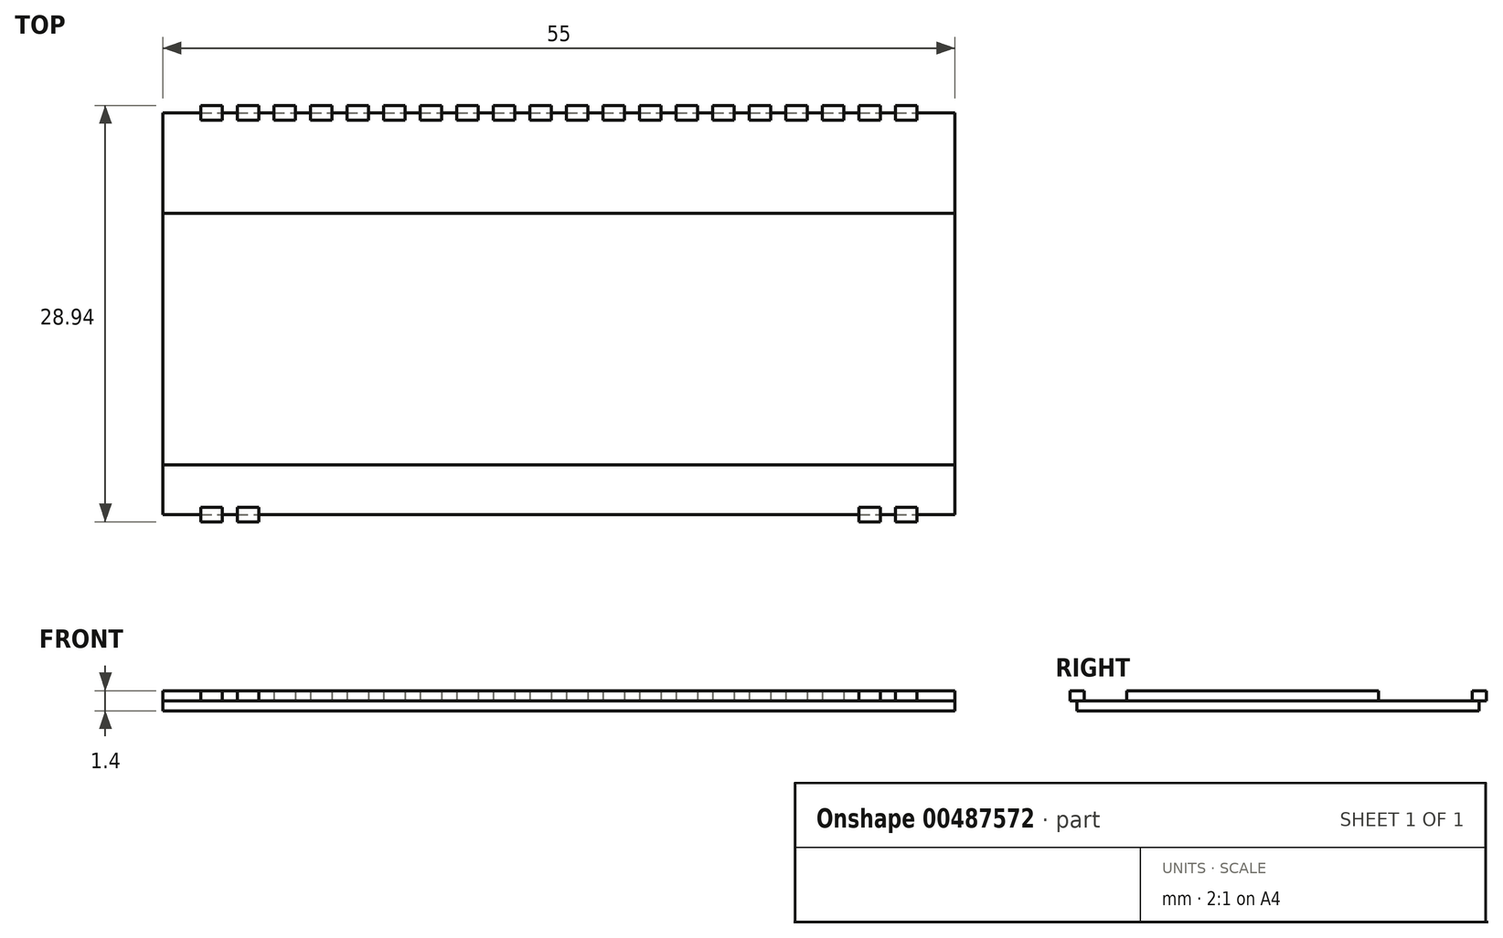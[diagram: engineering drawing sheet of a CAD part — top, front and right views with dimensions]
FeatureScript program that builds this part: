
annotation { "Feature Type Name" : "Feature", "Feature Type Description" : "" }
export const myFeature = defineFeature(function(context is Context, id is Id, definition is map)
    precondition{}
    {
        {
            var Q0;
            Q0=qCreatedBy(makeId("Top.planeOp"),FACE);
            var sketch = newSketch(context, id + "F0", { "sketchPlane" : qUnion([Q0])});
            skLineSegment(sketch, "E0.bottom", {"start": v(-27.5, 15.75) * mm, "end": v(27.5, 15.75) * mm});
            skLineSegment(sketch, "E0.top", {"start": v(-27.5, -12.2) * mm, "end": v(27.5, -12.2) * mm});
            skLineSegment(sketch, "E0.left", {"start": v(-27.5, 15.75) * mm, "end": v(-27.5, -12.2) * mm});
            skLineSegment(sketch, "E0.right", {"start": v(27.5, 15.75) * mm, "end": v(27.5, -12.2) * mm});
            skLineSegment(sketch, "E1", {"start": v(-27.5, 8.75) * mm, "end": v(27.5, 8.75) * mm});
            skLineSegment(sketch, "E2", {"start": v(-27.5, -8.75) * mm, "end": v(27.5, -8.75) * mm});
            skLineSegment(sketch, "E3.bottom", {"start": v(-24.08, 6.64) * mm, "end": v(24.08, 6.64) * mm});
            skLineSegment(sketch, "E3.top", {"start": v(-24.08, -6.63) * mm, "end": v(24.08, -6.64) * mm});
            skLineSegment(sketch, "E3.left", {"start": v(-24.09, 6.64) * mm, "end": v(-24.09, -6.64) * mm});
            skLineSegment(sketch, "E3.right", {"start": v(24.09, 6.64) * mm, "end": v(24.08, -6.64) * mm});
            skLineSegment(sketch, "E4", {"start": v(0, 15.75) * mm, "end": v(0, -12.2) * mm, "construction": true});
            skLineSegment(sketch, "E5", {"start": v(-24.09, 0) * mm, "end": v(24.09, 0) * mm, "construction": true});
            skLineSegment(sketch, "E6", {"start": v(0, 6.64) * mm, "end": v(0, -6.64) * mm, "construction": true});
            skLineSegment(sketch, "E7.bottom", {"start": v(-24.88, 16.25) * mm, "end": v(-23.38, 16.25) * mm});
            skLineSegment(sketch, "E7.top", {"start": v(-24.88, 15.25) * mm, "end": v(-23.38, 15.25) * mm});
            skLineSegment(sketch, "E7.left", {"start": v(-24.88, 16.25) * mm, "end": v(-24.88, 15.25) * mm});
            skLineSegment(sketch, "E7.right", {"start": v(-23.38, 16.25) * mm, "end": v(-23.38, 15.25) * mm});
            skLineSegment(sketch, "E8.bottom", {"start": v(-23.38, -12.7) * mm, "end": v(-24.88, -12.7) * mm});
            skLineSegment(sketch, "E8.top", {"start": v(-23.38, -11.7) * mm, "end": v(-24.88, -11.7) * mm});
            skLineSegment(sketch, "E8.left", {"start": v(-23.38, -12.7) * mm, "end": v(-23.38, -11.7) * mm});
            skLineSegment(sketch, "E8.right", {"start": v(-24.88, -12.7) * mm, "end": v(-24.88, -11.7) * mm});
            skLineSegment(sketch, "E9.1.0.0", {"start": v(-22.34, 15.25) * mm, "end": v(-20.84, 15.25) * mm});
            skLineSegment(sketch, "E9.1.0.1", {"start": v(-22.34, 16.25) * mm, "end": v(-20.84, 16.25) * mm});
            skLineSegment(sketch, "E9.1.0.2", {"start": v(-20.84, 16.25) * mm, "end": v(-20.84, 15.25) * mm});
            skLineSegment(sketch, "E9.1.0.3", {"start": v(-22.34, 16.25) * mm, "end": v(-22.34, 15.25) * mm});
            skLineSegment(sketch, "E9.2.0.0", {"start": v(-19.8, 15.25) * mm, "end": v(-18.3, 15.25) * mm});
            skLineSegment(sketch, "E9.2.0.1", {"start": v(-19.8, 16.25) * mm, "end": v(-18.3, 16.25) * mm});
            skLineSegment(sketch, "E9.2.0.2", {"start": v(-18.3, 16.25) * mm, "end": v(-18.3, 15.25) * mm});
            skLineSegment(sketch, "E9.2.0.3", {"start": v(-19.8, 16.25) * mm, "end": v(-19.8, 15.25) * mm});
            skLineSegment(sketch, "E9.3.0.0", {"start": v(-17.26, 15.25) * mm, "end": v(-15.76, 15.25) * mm});
            skLineSegment(sketch, "E9.3.0.1", {"start": v(-17.26, 16.25) * mm, "end": v(-15.76, 16.25) * mm});
            skLineSegment(sketch, "E9.3.0.2", {"start": v(-15.76, 16.25) * mm, "end": v(-15.76, 15.25) * mm});
            skLineSegment(sketch, "E9.3.0.3", {"start": v(-17.26, 16.25) * mm, "end": v(-17.26, 15.25) * mm});
            skLineSegment(sketch, "E9.4.0.0", {"start": v(-14.72, 15.25) * mm, "end": v(-13.22, 15.25) * mm});
            skLineSegment(sketch, "E9.4.0.1", {"start": v(-14.72, 16.25) * mm, "end": v(-13.22, 16.25) * mm});
            skLineSegment(sketch, "E9.4.0.2", {"start": v(-13.22, 16.25) * mm, "end": v(-13.22, 15.25) * mm});
            skLineSegment(sketch, "E9.4.0.3", {"start": v(-14.72, 16.25) * mm, "end": v(-14.72, 15.25) * mm});
            skLineSegment(sketch, "E9.5.0.0", {"start": v(-12.18, 15.25) * mm, "end": v(-10.68, 15.25) * mm});
            skLineSegment(sketch, "E9.5.0.1", {"start": v(-12.18, 16.25) * mm, "end": v(-10.68, 16.25) * mm});
            skLineSegment(sketch, "E9.5.0.2", {"start": v(-10.68, 16.25) * mm, "end": v(-10.68, 15.25) * mm});
            skLineSegment(sketch, "E9.5.0.3", {"start": v(-12.18, 16.25) * mm, "end": v(-12.18, 15.25) * mm});
            skLineSegment(sketch, "E9.6.0.0", {"start": v(-9.64, 15.25) * mm, "end": v(-8.14, 15.25) * mm});
            skLineSegment(sketch, "E9.6.0.1", {"start": v(-9.64, 16.25) * mm, "end": v(-8.14, 16.25) * mm});
            skLineSegment(sketch, "E9.6.0.2", {"start": v(-8.14, 16.25) * mm, "end": v(-8.14, 15.25) * mm});
            skLineSegment(sketch, "E9.6.0.3", {"start": v(-9.64, 16.25) * mm, "end": v(-9.64, 15.25) * mm});
            skLineSegment(sketch, "E9.7.0.0", {"start": v(-7.1, 15.25) * mm, "end": v(-5.6, 15.25) * mm});
            skLineSegment(sketch, "E9.7.0.1", {"start": v(-7.1, 16.25) * mm, "end": v(-5.6, 16.25) * mm});
            skLineSegment(sketch, "E9.7.0.2", {"start": v(-5.6, 16.25) * mm, "end": v(-5.6, 15.25) * mm});
            skLineSegment(sketch, "E9.7.0.3", {"start": v(-7.1, 16.25) * mm, "end": v(-7.1, 15.25) * mm});
            skLineSegment(sketch, "E9.8.0.0", {"start": v(-4.56, 15.25) * mm, "end": v(-3.06, 15.25) * mm});
            skLineSegment(sketch, "E9.8.0.1", {"start": v(-4.56, 16.25) * mm, "end": v(-3.06, 16.25) * mm});
            skLineSegment(sketch, "E9.8.0.2", {"start": v(-3.06, 16.25) * mm, "end": v(-3.06, 15.25) * mm});
            skLineSegment(sketch, "E9.8.0.3", {"start": v(-4.56, 16.25) * mm, "end": v(-4.56, 15.25) * mm});
            skLineSegment(sketch, "E9.9.0.0", {"start": v(-2.02, 15.25) * mm, "end": v(-0.52, 15.25) * mm});
            skLineSegment(sketch, "E9.9.0.1", {"start": v(-2.02, 16.25) * mm, "end": v(-0.52, 16.25) * mm});
            skLineSegment(sketch, "E9.9.0.2", {"start": v(-0.52, 16.25) * mm, "end": v(-0.52, 15.25) * mm});
            skLineSegment(sketch, "E9.9.0.3", {"start": v(-2.02, 16.25) * mm, "end": v(-2.02, 15.25) * mm});
            skLineSegment(sketch, "E9.10.0.0", {"start": v(0.52, 15.25) * mm, "end": v(2.02, 15.25) * mm});
            skLineSegment(sketch, "E9.10.0.1", {"start": v(0.52, 16.25) * mm, "end": v(2.02, 16.25) * mm});
            skLineSegment(sketch, "E9.10.0.2", {"start": v(2.02, 16.25) * mm, "end": v(2.02, 15.25) * mm});
            skLineSegment(sketch, "E9.10.0.3", {"start": v(0.52, 16.25) * mm, "end": v(0.52, 15.25) * mm});
            skLineSegment(sketch, "E9.11.0.0", {"start": v(3.06, 15.25) * mm, "end": v(4.56, 15.25) * mm});
            skLineSegment(sketch, "E9.11.0.1", {"start": v(3.06, 16.25) * mm, "end": v(4.56, 16.25) * mm});
            skLineSegment(sketch, "E9.11.0.2", {"start": v(4.56, 16.25) * mm, "end": v(4.56, 15.25) * mm});
            skLineSegment(sketch, "E9.11.0.3", {"start": v(3.06, 16.25) * mm, "end": v(3.06, 15.25) * mm});
            skLineSegment(sketch, "E9.12.0.0", {"start": v(5.6, 15.25) * mm, "end": v(7.1, 15.25) * mm});
            skLineSegment(sketch, "E9.12.0.1", {"start": v(5.6, 16.25) * mm, "end": v(7.1, 16.25) * mm});
            skLineSegment(sketch, "E9.12.0.2", {"start": v(7.1, 16.25) * mm, "end": v(7.1, 15.25) * mm});
            skLineSegment(sketch, "E9.12.0.3", {"start": v(5.6, 16.25) * mm, "end": v(5.6, 15.25) * mm});
            skLineSegment(sketch, "E9.13.0.0", {"start": v(8.14, 15.25) * mm, "end": v(9.64, 15.25) * mm});
            skLineSegment(sketch, "E9.13.0.1", {"start": v(8.14, 16.25) * mm, "end": v(9.64, 16.25) * mm});
            skLineSegment(sketch, "E9.13.0.2", {"start": v(9.64, 16.25) * mm, "end": v(9.64, 15.25) * mm});
            skLineSegment(sketch, "E9.13.0.3", {"start": v(8.14, 16.25) * mm, "end": v(8.14, 15.25) * mm});
            skLineSegment(sketch, "E9.14.0.0", {"start": v(10.68, 15.25) * mm, "end": v(12.18, 15.25) * mm});
            skLineSegment(sketch, "E9.14.0.1", {"start": v(10.68, 16.25) * mm, "end": v(12.18, 16.25) * mm});
            skLineSegment(sketch, "E9.14.0.2", {"start": v(12.18, 16.25) * mm, "end": v(12.18, 15.25) * mm});
            skLineSegment(sketch, "E9.14.0.3", {"start": v(10.68, 16.25) * mm, "end": v(10.68, 15.25) * mm});
            skLineSegment(sketch, "E9.15.0.0", {"start": v(13.22, 15.25) * mm, "end": v(14.72, 15.25) * mm});
            skLineSegment(sketch, "E9.15.0.1", {"start": v(13.22, 16.25) * mm, "end": v(14.72, 16.25) * mm});
            skLineSegment(sketch, "E9.15.0.2", {"start": v(14.72, 16.25) * mm, "end": v(14.72, 15.25) * mm});
            skLineSegment(sketch, "E9.15.0.3", {"start": v(13.22, 16.25) * mm, "end": v(13.22, 15.25) * mm});
            skLineSegment(sketch, "E9.16.0.0", {"start": v(15.76, 15.25) * mm, "end": v(17.26, 15.25) * mm});
            skLineSegment(sketch, "E9.16.0.1", {"start": v(15.76, 16.25) * mm, "end": v(17.26, 16.25) * mm});
            skLineSegment(sketch, "E9.16.0.2", {"start": v(17.26, 16.25) * mm, "end": v(17.26, 15.25) * mm});
            skLineSegment(sketch, "E9.16.0.3", {"start": v(15.76, 16.25) * mm, "end": v(15.76, 15.25) * mm});
            skLineSegment(sketch, "E9.17.0.0", {"start": v(18.3, 15.25) * mm, "end": v(19.8, 15.25) * mm});
            skLineSegment(sketch, "E9.17.0.1", {"start": v(18.3, 16.25) * mm, "end": v(19.8, 16.25) * mm});
            skLineSegment(sketch, "E9.17.0.2", {"start": v(19.8, 16.25) * mm, "end": v(19.8, 15.25) * mm});
            skLineSegment(sketch, "E9.17.0.3", {"start": v(18.3, 16.25) * mm, "end": v(18.3, 15.25) * mm});
            skLineSegment(sketch, "E9.18.0.0", {"start": v(20.84, 15.25) * mm, "end": v(22.34, 15.25) * mm});
            skLineSegment(sketch, "E9.18.0.1", {"start": v(20.84, 16.25) * mm, "end": v(22.34, 16.25) * mm});
            skLineSegment(sketch, "E9.18.0.2", {"start": v(22.34, 16.25) * mm, "end": v(22.34, 15.25) * mm});
            skLineSegment(sketch, "E9.18.0.3", {"start": v(20.84, 16.25) * mm, "end": v(20.84, 15.25) * mm});
            skLineSegment(sketch, "E9.19.0.0", {"start": v(23.38, 15.25) * mm, "end": v(24.88, 15.25) * mm});
            skLineSegment(sketch, "E9.19.0.1", {"start": v(23.38, 16.25) * mm, "end": v(24.88, 16.25) * mm});
            skLineSegment(sketch, "E9.19.0.2", {"start": v(24.88, 16.25) * mm, "end": v(24.88, 15.25) * mm});
            skLineSegment(sketch, "E9.19.0.3", {"start": v(23.38, 16.25) * mm, "end": v(23.38, 15.25) * mm});
            skLineSegment(sketch, "E9.direction1", {"start": v(-24.88, 15.25) * mm, "end": v(-22.34, 15.25) * mm, "construction": true});
            skLineSegment(sketch, "E10.1.0.0", {"start": v(-20.84, -11.7) * mm, "end": v(-22.34, -11.7) * mm});
            skLineSegment(sketch, "E10.1.0.1", {"start": v(-22.34, -12.7) * mm, "end": v(-22.34, -11.7) * mm});
            skLineSegment(sketch, "E10.1.0.2", {"start": v(-20.84, -12.7) * mm, "end": v(-22.34, -12.7) * mm});
            skLineSegment(sketch, "E10.1.0.3", {"start": v(-20.84, -12.7) * mm, "end": v(-20.84, -11.7) * mm});
            skLineSegment(sketch, "E10.18.0.0", {"start": v(22.34, -11.7) * mm, "end": v(20.84, -11.7) * mm});
            skLineSegment(sketch, "E10.18.0.1", {"start": v(20.84, -12.7) * mm, "end": v(20.84, -11.7) * mm});
            skLineSegment(sketch, "E10.18.0.2", {"start": v(22.34, -12.7) * mm, "end": v(20.84, -12.7) * mm});
            skLineSegment(sketch, "E10.18.0.3", {"start": v(22.34, -12.7) * mm, "end": v(22.34, -11.7) * mm});
            skLineSegment(sketch, "E10.19.0.0", {"start": v(24.88, -11.7) * mm, "end": v(23.38, -11.7) * mm});
            skLineSegment(sketch, "E10.19.0.1", {"start": v(23.38, -12.7) * mm, "end": v(23.38, -11.7) * mm});
            skLineSegment(sketch, "E10.19.0.2", {"start": v(24.88, -12.7) * mm, "end": v(23.38, -12.7) * mm});
            skLineSegment(sketch, "E10.19.0.3", {"start": v(24.88, -12.7) * mm, "end": v(24.88, -11.7) * mm});
            skLineSegment(sketch, "E10.direction1", {"start": v(-24.88, -11.7) * mm, "end": v(-22.34, -11.7) * mm, "construction": true});
            skSolve(sketch);
        }
        {
            var Q0;
            {var subQ5=sQuery(id+"F0.wireOp",EDGE,"E7.top");Q0=makeQuery(id+"F0.imprint","IMPRINT",FACE,{"disambiguationData":[TD([[makeQuery(id+"F0.imprint","IMPRINT",EDGE,{"derivedFrom":subQ5}),1.0]])]});}
            var Q1;
            {var subQ1=sQuery(id+"F0.wireOp",EDGE,"E1");Q1=makeQuery(id+"F0.imprint","IMPRINT",FACE,{"disambiguationData":[TD([[makeQuery(id+"F0.imprint","IMPRINT",EDGE,{"derivedFrom":subQ1}),-1.0]])]});}
            var Q2;
            {var subQ0=sQuery(id+"F0.wireOp",EDGE,"E0.top");Q2=makeQuery(id+"F0.imprint","IMPRINT",FACE,{"disambiguationData":[TD([[makeQuery(id+"F0.imprint","IMPRINT",EDGE,{"derivedFrom":subQ0}),1.0]])]});}
            var Q3;
            Q3=makeQuery(id+"F0.imprint","IMPRINT",FACE,{"disambiguationData":[TD([[makeQuery(id+"F0.imprint","IMPRINT",EDGE,{"derivedFrom":sQuery(id+"F0.wireOp",EDGE,"E3.bottom")}),-1.0]])]});
            var Q4;
            {var subQ3=sQuery(id+"F0.wireOp",EDGE,"E1");Q4=makeQuery(id+"F0.imprint","IMPRINT",FACE,{"disambiguationData":[TD([[makeQuery(id+"F0.imprint","IMPRINT",EDGE,{"derivedFrom":subQ3}),1.0]])]});}
            var Q5;
            {var subQ5=sQuery(id+"F0.wireOp",EDGE,"E9.1.0.0");Q5=makeQuery(id+"F0.imprint","IMPRINT",FACE,{"disambiguationData":[TD([[makeQuery(id+"F0.imprint","IMPRINT",EDGE,{"derivedFrom":subQ5}),1.0]])]});}
            var Q6;
            {var subQ5=sQuery(id+"F0.wireOp",EDGE,"E9.2.0.0");Q6=makeQuery(id+"F0.imprint","IMPRINT",FACE,{"disambiguationData":[TD([[makeQuery(id+"F0.imprint","IMPRINT",EDGE,{"derivedFrom":subQ5}),1.0]])]});}
            var Q7;
            {var subQ5=sQuery(id+"F0.wireOp",EDGE,"E9.3.0.0");Q7=makeQuery(id+"F0.imprint","IMPRINT",FACE,{"disambiguationData":[TD([[makeQuery(id+"F0.imprint","IMPRINT",EDGE,{"derivedFrom":subQ5}),1.0]])]});}
            var Q8;
            {var subQ5=sQuery(id+"F0.wireOp",EDGE,"E9.4.0.0");Q8=makeQuery(id+"F0.imprint","IMPRINT",FACE,{"disambiguationData":[TD([[makeQuery(id+"F0.imprint","IMPRINT",EDGE,{"derivedFrom":subQ5}),1.0]])]});}
            var Q9;
            {var subQ5=sQuery(id+"F0.wireOp",EDGE,"E9.5.0.0");Q9=makeQuery(id+"F0.imprint","IMPRINT",FACE,{"disambiguationData":[TD([[makeQuery(id+"F0.imprint","IMPRINT",EDGE,{"derivedFrom":subQ5}),1.0]])]});}
            var Q10;
            {var subQ5=sQuery(id+"F0.wireOp",EDGE,"E9.6.0.0");Q10=makeQuery(id+"F0.imprint","IMPRINT",FACE,{"disambiguationData":[TD([[makeQuery(id+"F0.imprint","IMPRINT",EDGE,{"derivedFrom":subQ5}),1.0]])]});}
            var Q11;
            {var subQ5=sQuery(id+"F0.wireOp",EDGE,"E9.7.0.0");Q11=makeQuery(id+"F0.imprint","IMPRINT",FACE,{"disambiguationData":[TD([[makeQuery(id+"F0.imprint","IMPRINT",EDGE,{"derivedFrom":subQ5}),1.0]])]});}
            var Q12;
            {var subQ5=sQuery(id+"F0.wireOp",EDGE,"E9.8.0.0");Q12=makeQuery(id+"F0.imprint","IMPRINT",FACE,{"disambiguationData":[TD([[makeQuery(id+"F0.imprint","IMPRINT",EDGE,{"derivedFrom":subQ5}),1.0]])]});}
            var Q13;
            {var subQ5=sQuery(id+"F0.wireOp",EDGE,"E9.9.0.0");Q13=makeQuery(id+"F0.imprint","IMPRINT",FACE,{"disambiguationData":[TD([[makeQuery(id+"F0.imprint","IMPRINT",EDGE,{"derivedFrom":subQ5}),1.0]])]});}
            var Q14;
            {var subQ5=sQuery(id+"F0.wireOp",EDGE,"E9.10.0.0");Q14=makeQuery(id+"F0.imprint","IMPRINT",FACE,{"disambiguationData":[TD([[makeQuery(id+"F0.imprint","IMPRINT",EDGE,{"derivedFrom":subQ5}),1.0]])]});}
            var Q15;
            {var subQ5=sQuery(id+"F0.wireOp",EDGE,"E9.11.0.0");Q15=makeQuery(id+"F0.imprint","IMPRINT",FACE,{"disambiguationData":[TD([[makeQuery(id+"F0.imprint","IMPRINT",EDGE,{"derivedFrom":subQ5}),1.0]])]});}
            var Q16;
            {var subQ5=sQuery(id+"F0.wireOp",EDGE,"E9.12.0.0");Q16=makeQuery(id+"F0.imprint","IMPRINT",FACE,{"disambiguationData":[TD([[makeQuery(id+"F0.imprint","IMPRINT",EDGE,{"derivedFrom":subQ5}),1.0]])]});}
            var Q17;
            {var subQ5=sQuery(id+"F0.wireOp",EDGE,"E9.13.0.0");Q17=makeQuery(id+"F0.imprint","IMPRINT",FACE,{"disambiguationData":[TD([[makeQuery(id+"F0.imprint","IMPRINT",EDGE,{"derivedFrom":subQ5}),1.0]])]});}
            var Q18;
            {var subQ5=sQuery(id+"F0.wireOp",EDGE,"E9.14.0.0");Q18=makeQuery(id+"F0.imprint","IMPRINT",FACE,{"disambiguationData":[TD([[makeQuery(id+"F0.imprint","IMPRINT",EDGE,{"derivedFrom":subQ5}),1.0]])]});}
            var Q19;
            {var subQ5=sQuery(id+"F0.wireOp",EDGE,"E9.15.0.0");Q19=makeQuery(id+"F0.imprint","IMPRINT",FACE,{"disambiguationData":[TD([[makeQuery(id+"F0.imprint","IMPRINT",EDGE,{"derivedFrom":subQ5}),1.0]])]});}
            var Q20;
            {var subQ5=sQuery(id+"F0.wireOp",EDGE,"E9.16.0.0");Q20=makeQuery(id+"F0.imprint","IMPRINT",FACE,{"disambiguationData":[TD([[makeQuery(id+"F0.imprint","IMPRINT",EDGE,{"derivedFrom":subQ5}),1.0]])]});}
            var Q21;
            {var subQ5=sQuery(id+"F0.wireOp",EDGE,"E9.17.0.0");Q21=makeQuery(id+"F0.imprint","IMPRINT",FACE,{"disambiguationData":[TD([[makeQuery(id+"F0.imprint","IMPRINT",EDGE,{"derivedFrom":subQ5}),1.0]])]});}
            var Q22;
            {var subQ5=sQuery(id+"F0.wireOp",EDGE,"E9.18.0.0");Q22=makeQuery(id+"F0.imprint","IMPRINT",FACE,{"disambiguationData":[TD([[makeQuery(id+"F0.imprint","IMPRINT",EDGE,{"derivedFrom":subQ5}),1.0]])]});}
            var Q23;
            {var subQ5=sQuery(id+"F0.wireOp",EDGE,"E9.19.0.0");Q23=makeQuery(id+"F0.imprint","IMPRINT",FACE,{"disambiguationData":[TD([[makeQuery(id+"F0.imprint","IMPRINT",EDGE,{"derivedFrom":subQ5}),1.0]])]});}
            var Q24;
            {var subQ5=sQuery(id+"F0.wireOp",EDGE,"E10.19.0.0");Q24=makeQuery(id+"F0.imprint","IMPRINT",FACE,{"disambiguationData":[TD([[makeQuery(id+"F0.imprint","IMPRINT",EDGE,{"derivedFrom":subQ5}),1.0]])]});}
            var Q25;
            {var subQ5=sQuery(id+"F0.wireOp",EDGE,"E10.18.0.0");Q25=makeQuery(id+"F0.imprint","IMPRINT",FACE,{"disambiguationData":[TD([[makeQuery(id+"F0.imprint","IMPRINT",EDGE,{"derivedFrom":subQ5}),1.0]])]});}
            var Q26;
            {var subQ5=sQuery(id+"F0.wireOp",EDGE,"E10.1.0.0");Q26=makeQuery(id+"F0.imprint","IMPRINT",FACE,{"disambiguationData":[TD([[makeQuery(id+"F0.imprint","IMPRINT",EDGE,{"derivedFrom":subQ5}),1.0]])]});}
            var Q27;
            {var subQ5=sQuery(id+"F0.wireOp",EDGE,"E8.top");Q27=makeQuery(id+"F0.imprint","IMPRINT",FACE,{"disambiguationData":[TD([[makeQuery(id+"F0.imprint","IMPRINT",EDGE,{"derivedFrom":subQ5}),1.0]])]});}
            extrude(context, id + "F1", {"entities" : qUnion([Q0, Q1, Q2, Q3, Q4, Q5, Q6, Q7, Q8, Q9, Q10, Q11, Q12, Q13, Q14, Q15, Q16, Q17, Q18, Q19, Q20, Q21, Q22, Q23, Q24, Q25, Q26, Q27]), "oppositeDirection" : true, "depth" : 0.7 * mm});
        }
        {
            var Q0;
            Q0=makeQuery(id+"F0.imprint","IMPRINT",FACE,{"disambiguationData":[TD([[makeQuery(id+"F0.imprint","IMPRINT",EDGE,{"derivedFrom":sQuery(id+"F0.wireOp",EDGE,"E3.bottom")}),-1.0]])]});
            var Q1;
            {var subQ1=sQuery(id+"F0.wireOp",EDGE,"E1");Q1=makeQuery(id+"F0.imprint","IMPRINT",FACE,{"disambiguationData":[TD([[makeQuery(id+"F0.imprint","IMPRINT",EDGE,{"derivedFrom":subQ1}),-1.0]])]});}
            extrude(context, id + "F2", {"entities" : qUnion([Q0, Q1]), "depth" : 0.7 * mm});
        }
        {
            var Q0;
            {var subQ5=sQuery(id+"F0.wireOp",EDGE,"E7.top");Q0=makeQuery(id+"F0.imprint","IMPRINT",FACE,{"disambiguationData":[TD([[makeQuery(id+"F0.imprint","IMPRINT",EDGE,{"derivedFrom":subQ5}),1.0]])]});}
            var Q1;
            {var subQ5=sQuery(id+"F0.wireOp",EDGE,"E7.bottom");Q1=makeQuery(id+"F0.imprint","IMPRINT",FACE,{"disambiguationData":[TD([[makeQuery(id+"F0.imprint","IMPRINT",EDGE,{"derivedFrom":subQ5}),-1.0]])]});}
            var Q2;
            {var subQ5=sQuery(id+"F0.wireOp",EDGE,"E9.1.0.1");Q2=makeQuery(id+"F0.imprint","IMPRINT",FACE,{"disambiguationData":[TD([[makeQuery(id+"F0.imprint","IMPRINT",EDGE,{"derivedFrom":subQ5}),-1.0]])]});}
            var Q3;
            {var subQ5=sQuery(id+"F0.wireOp",EDGE,"E9.1.0.0");Q3=makeQuery(id+"F0.imprint","IMPRINT",FACE,{"disambiguationData":[TD([[makeQuery(id+"F0.imprint","IMPRINT",EDGE,{"derivedFrom":subQ5}),1.0]])]});}
            var Q4;
            {var subQ5=sQuery(id+"F0.wireOp",EDGE,"E9.2.0.0");Q4=makeQuery(id+"F0.imprint","IMPRINT",FACE,{"disambiguationData":[TD([[makeQuery(id+"F0.imprint","IMPRINT",EDGE,{"derivedFrom":subQ5}),1.0]])]});}
            var Q5;
            {var subQ5=sQuery(id+"F0.wireOp",EDGE,"E9.2.0.1");Q5=makeQuery(id+"F0.imprint","IMPRINT",FACE,{"disambiguationData":[TD([[makeQuery(id+"F0.imprint","IMPRINT",EDGE,{"derivedFrom":subQ5}),-1.0]])]});}
            var Q6;
            {var subQ5=sQuery(id+"F0.wireOp",EDGE,"E9.3.0.1");Q6=makeQuery(id+"F0.imprint","IMPRINT",FACE,{"disambiguationData":[TD([[makeQuery(id+"F0.imprint","IMPRINT",EDGE,{"derivedFrom":subQ5}),-1.0]])]});}
            var Q7;
            {var subQ5=sQuery(id+"F0.wireOp",EDGE,"E9.3.0.0");Q7=makeQuery(id+"F0.imprint","IMPRINT",FACE,{"disambiguationData":[TD([[makeQuery(id+"F0.imprint","IMPRINT",EDGE,{"derivedFrom":subQ5}),1.0]])]});}
            var Q8;
            {var subQ5=sQuery(id+"F0.wireOp",EDGE,"E9.4.0.0");Q8=makeQuery(id+"F0.imprint","IMPRINT",FACE,{"disambiguationData":[TD([[makeQuery(id+"F0.imprint","IMPRINT",EDGE,{"derivedFrom":subQ5}),1.0]])]});}
            var Q9;
            {var subQ5=sQuery(id+"F0.wireOp",EDGE,"E9.4.0.1");Q9=makeQuery(id+"F0.imprint","IMPRINT",FACE,{"disambiguationData":[TD([[makeQuery(id+"F0.imprint","IMPRINT",EDGE,{"derivedFrom":subQ5}),-1.0]])]});}
            var Q10;
            {var subQ5=sQuery(id+"F0.wireOp",EDGE,"E9.5.0.0");Q10=makeQuery(id+"F0.imprint","IMPRINT",FACE,{"disambiguationData":[TD([[makeQuery(id+"F0.imprint","IMPRINT",EDGE,{"derivedFrom":subQ5}),1.0]])]});}
            var Q11;
            {var subQ5=sQuery(id+"F0.wireOp",EDGE,"E9.5.0.1");Q11=makeQuery(id+"F0.imprint","IMPRINT",FACE,{"disambiguationData":[TD([[makeQuery(id+"F0.imprint","IMPRINT",EDGE,{"derivedFrom":subQ5}),-1.0]])]});}
            var Q12;
            {var subQ5=sQuery(id+"F0.wireOp",EDGE,"E9.6.0.0");Q12=makeQuery(id+"F0.imprint","IMPRINT",FACE,{"disambiguationData":[TD([[makeQuery(id+"F0.imprint","IMPRINT",EDGE,{"derivedFrom":subQ5}),1.0]])]});}
            var Q13;
            {var subQ5=sQuery(id+"F0.wireOp",EDGE,"E9.6.0.1");Q13=makeQuery(id+"F0.imprint","IMPRINT",FACE,{"disambiguationData":[TD([[makeQuery(id+"F0.imprint","IMPRINT",EDGE,{"derivedFrom":subQ5}),-1.0]])]});}
            var Q14;
            {var subQ5=sQuery(id+"F0.wireOp",EDGE,"E9.7.0.0");Q14=makeQuery(id+"F0.imprint","IMPRINT",FACE,{"disambiguationData":[TD([[makeQuery(id+"F0.imprint","IMPRINT",EDGE,{"derivedFrom":subQ5}),1.0]])]});}
            var Q15;
            {var subQ5=sQuery(id+"F0.wireOp",EDGE,"E9.7.0.1");Q15=makeQuery(id+"F0.imprint","IMPRINT",FACE,{"disambiguationData":[TD([[makeQuery(id+"F0.imprint","IMPRINT",EDGE,{"derivedFrom":subQ5}),-1.0]])]});}
            var Q16;
            {var subQ5=sQuery(id+"F0.wireOp",EDGE,"E9.8.0.0");Q16=makeQuery(id+"F0.imprint","IMPRINT",FACE,{"disambiguationData":[TD([[makeQuery(id+"F0.imprint","IMPRINT",EDGE,{"derivedFrom":subQ5}),1.0]])]});}
            var Q17;
            {var subQ5=sQuery(id+"F0.wireOp",EDGE,"E9.8.0.1");Q17=makeQuery(id+"F0.imprint","IMPRINT",FACE,{"disambiguationData":[TD([[makeQuery(id+"F0.imprint","IMPRINT",EDGE,{"derivedFrom":subQ5}),-1.0]])]});}
            var Q18;
            {var subQ5=sQuery(id+"F0.wireOp",EDGE,"E9.9.0.1");Q18=makeQuery(id+"F0.imprint","IMPRINT",FACE,{"disambiguationData":[TD([[makeQuery(id+"F0.imprint","IMPRINT",EDGE,{"derivedFrom":subQ5}),-1.0]])]});}
            var Q19;
            {var subQ5=sQuery(id+"F0.wireOp",EDGE,"E9.9.0.0");Q19=makeQuery(id+"F0.imprint","IMPRINT",FACE,{"disambiguationData":[TD([[makeQuery(id+"F0.imprint","IMPRINT",EDGE,{"derivedFrom":subQ5}),1.0]])]});}
            var Q20;
            {var subQ5=sQuery(id+"F0.wireOp",EDGE,"E9.10.0.0");Q20=makeQuery(id+"F0.imprint","IMPRINT",FACE,{"disambiguationData":[TD([[makeQuery(id+"F0.imprint","IMPRINT",EDGE,{"derivedFrom":subQ5}),1.0]])]});}
            var Q21;
            {var subQ5=sQuery(id+"F0.wireOp",EDGE,"E9.10.0.1");Q21=makeQuery(id+"F0.imprint","IMPRINT",FACE,{"disambiguationData":[TD([[makeQuery(id+"F0.imprint","IMPRINT",EDGE,{"derivedFrom":subQ5}),-1.0]])]});}
            var Q22;
            {var subQ5=sQuery(id+"F0.wireOp",EDGE,"E9.11.0.0");Q22=makeQuery(id+"F0.imprint","IMPRINT",FACE,{"disambiguationData":[TD([[makeQuery(id+"F0.imprint","IMPRINT",EDGE,{"derivedFrom":subQ5}),1.0]])]});}
            var Q23;
            {var subQ5=sQuery(id+"F0.wireOp",EDGE,"E9.11.0.1");Q23=makeQuery(id+"F0.imprint","IMPRINT",FACE,{"disambiguationData":[TD([[makeQuery(id+"F0.imprint","IMPRINT",EDGE,{"derivedFrom":subQ5}),-1.0]])]});}
            var Q24;
            {var subQ5=sQuery(id+"F0.wireOp",EDGE,"E9.12.0.1");Q24=makeQuery(id+"F0.imprint","IMPRINT",FACE,{"disambiguationData":[TD([[makeQuery(id+"F0.imprint","IMPRINT",EDGE,{"derivedFrom":subQ5}),-1.0]])]});}
            var Q25;
            {var subQ5=sQuery(id+"F0.wireOp",EDGE,"E9.13.0.0");Q25=makeQuery(id+"F0.imprint","IMPRINT",FACE,{"disambiguationData":[TD([[makeQuery(id+"F0.imprint","IMPRINT",EDGE,{"derivedFrom":subQ5}),1.0]])]});}
            var Q26;
            {var subQ5=sQuery(id+"F0.wireOp",EDGE,"E9.13.0.1");Q26=makeQuery(id+"F0.imprint","IMPRINT",FACE,{"disambiguationData":[TD([[makeQuery(id+"F0.imprint","IMPRINT",EDGE,{"derivedFrom":subQ5}),-1.0]])]});}
            var Q27;
            {var subQ5=sQuery(id+"F0.wireOp",EDGE,"E9.12.0.0");Q27=makeQuery(id+"F0.imprint","IMPRINT",FACE,{"disambiguationData":[TD([[makeQuery(id+"F0.imprint","IMPRINT",EDGE,{"derivedFrom":subQ5}),1.0]])]});}
            var Q28;
            {var subQ5=sQuery(id+"F0.wireOp",EDGE,"E9.14.0.0");Q28=makeQuery(id+"F0.imprint","IMPRINT",FACE,{"disambiguationData":[TD([[makeQuery(id+"F0.imprint","IMPRINT",EDGE,{"derivedFrom":subQ5}),1.0]])]});}
            var Q29;
            {var subQ5=sQuery(id+"F0.wireOp",EDGE,"E9.14.0.1");Q29=makeQuery(id+"F0.imprint","IMPRINT",FACE,{"disambiguationData":[TD([[makeQuery(id+"F0.imprint","IMPRINT",EDGE,{"derivedFrom":subQ5}),-1.0]])]});}
            var Q30;
            {var subQ5=sQuery(id+"F0.wireOp",EDGE,"E9.15.0.0");Q30=makeQuery(id+"F0.imprint","IMPRINT",FACE,{"disambiguationData":[TD([[makeQuery(id+"F0.imprint","IMPRINT",EDGE,{"derivedFrom":subQ5}),1.0]])]});}
            var Q31;
            {var subQ5=sQuery(id+"F0.wireOp",EDGE,"E9.15.0.1");Q31=makeQuery(id+"F0.imprint","IMPRINT",FACE,{"disambiguationData":[TD([[makeQuery(id+"F0.imprint","IMPRINT",EDGE,{"derivedFrom":subQ5}),-1.0]])]});}
            var Q32;
            {var subQ5=sQuery(id+"F0.wireOp",EDGE,"E9.16.0.0");Q32=makeQuery(id+"F0.imprint","IMPRINT",FACE,{"disambiguationData":[TD([[makeQuery(id+"F0.imprint","IMPRINT",EDGE,{"derivedFrom":subQ5}),1.0]])]});}
            var Q33;
            {var subQ5=sQuery(id+"F0.wireOp",EDGE,"E9.16.0.1");Q33=makeQuery(id+"F0.imprint","IMPRINT",FACE,{"disambiguationData":[TD([[makeQuery(id+"F0.imprint","IMPRINT",EDGE,{"derivedFrom":subQ5}),-1.0]])]});}
            var Q34;
            {var subQ5=sQuery(id+"F0.wireOp",EDGE,"E9.17.0.0");Q34=makeQuery(id+"F0.imprint","IMPRINT",FACE,{"disambiguationData":[TD([[makeQuery(id+"F0.imprint","IMPRINT",EDGE,{"derivedFrom":subQ5}),1.0]])]});}
            var Q35;
            {var subQ5=sQuery(id+"F0.wireOp",EDGE,"E9.17.0.1");Q35=makeQuery(id+"F0.imprint","IMPRINT",FACE,{"disambiguationData":[TD([[makeQuery(id+"F0.imprint","IMPRINT",EDGE,{"derivedFrom":subQ5}),-1.0]])]});}
            var Q36;
            {var subQ5=sQuery(id+"F0.wireOp",EDGE,"E9.18.0.0");Q36=makeQuery(id+"F0.imprint","IMPRINT",FACE,{"disambiguationData":[TD([[makeQuery(id+"F0.imprint","IMPRINT",EDGE,{"derivedFrom":subQ5}),1.0]])]});}
            var Q37;
            {var subQ5=sQuery(id+"F0.wireOp",EDGE,"E9.18.0.1");Q37=makeQuery(id+"F0.imprint","IMPRINT",FACE,{"disambiguationData":[TD([[makeQuery(id+"F0.imprint","IMPRINT",EDGE,{"derivedFrom":subQ5}),-1.0]])]});}
            var Q38;
            {var subQ5=sQuery(id+"F0.wireOp",EDGE,"E9.19.0.0");Q38=makeQuery(id+"F0.imprint","IMPRINT",FACE,{"disambiguationData":[TD([[makeQuery(id+"F0.imprint","IMPRINT",EDGE,{"derivedFrom":subQ5}),1.0]])]});}
            var Q39;
            {var subQ5=sQuery(id+"F0.wireOp",EDGE,"E9.19.0.1");Q39=makeQuery(id+"F0.imprint","IMPRINT",FACE,{"disambiguationData":[TD([[makeQuery(id+"F0.imprint","IMPRINT",EDGE,{"derivedFrom":subQ5}),-1.0]])]});}
            var Q40;
            {var subQ5=sQuery(id+"F0.wireOp",EDGE,"E10.19.0.0");Q40=makeQuery(id+"F0.imprint","IMPRINT",FACE,{"disambiguationData":[TD([[makeQuery(id+"F0.imprint","IMPRINT",EDGE,{"derivedFrom":subQ5}),1.0]])]});}
            var Q41;
            {var subQ5=sQuery(id+"F0.wireOp",EDGE,"E10.19.0.2");Q41=makeQuery(id+"F0.imprint","IMPRINT",FACE,{"disambiguationData":[TD([[makeQuery(id+"F0.imprint","IMPRINT",EDGE,{"derivedFrom":subQ5}),-1.0]])]});}
            var Q42;
            {var subQ5=sQuery(id+"F0.wireOp",EDGE,"E10.18.0.0");Q42=makeQuery(id+"F0.imprint","IMPRINT",FACE,{"disambiguationData":[TD([[makeQuery(id+"F0.imprint","IMPRINT",EDGE,{"derivedFrom":subQ5}),1.0]])]});}
            var Q43;
            {var subQ5=sQuery(id+"F0.wireOp",EDGE,"E10.18.0.2");Q43=makeQuery(id+"F0.imprint","IMPRINT",FACE,{"disambiguationData":[TD([[makeQuery(id+"F0.imprint","IMPRINT",EDGE,{"derivedFrom":subQ5}),-1.0]])]});}
            var Q44;
            {var subQ5=sQuery(id+"F0.wireOp",EDGE,"E8.top");Q44=makeQuery(id+"F0.imprint","IMPRINT",FACE,{"disambiguationData":[TD([[makeQuery(id+"F0.imprint","IMPRINT",EDGE,{"derivedFrom":subQ5}),1.0]])]});}
            var Q45;
            {var subQ5=sQuery(id+"F0.wireOp",EDGE,"E8.bottom");Q45=makeQuery(id+"F0.imprint","IMPRINT",FACE,{"disambiguationData":[TD([[makeQuery(id+"F0.imprint","IMPRINT",EDGE,{"derivedFrom":subQ5}),-1.0]])]});}
            var Q46;
            {var subQ5=sQuery(id+"F0.wireOp",EDGE,"E10.1.0.0");Q46=makeQuery(id+"F0.imprint","IMPRINT",FACE,{"disambiguationData":[TD([[makeQuery(id+"F0.imprint","IMPRINT",EDGE,{"derivedFrom":subQ5}),1.0]])]});}
            var Q47;
            {var subQ5=sQuery(id+"F0.wireOp",EDGE,"E10.1.0.2");Q47=makeQuery(id+"F0.imprint","IMPRINT",FACE,{"disambiguationData":[TD([[makeQuery(id+"F0.imprint","IMPRINT",EDGE,{"derivedFrom":subQ5}),-1.0]])]});}
            extrude(context, id + "F3", {"entities" : qUnion([Q0, Q1, Q2, Q3, Q4, Q5, Q6, Q7, Q8, Q9, Q10, Q11, Q12, Q13, Q14, Q15, Q16, Q17, Q18, Q19, Q20, Q21, Q22, Q23, Q24, Q25, Q26, Q27, Q28, Q29, Q30, Q31, Q32, Q33, Q34, Q35, Q36, Q37, Q38, Q39, Q40, Q41, Q42, Q43, Q44, Q45, Q46, Q47]), "operationType" : NewBodyOperationType.ADD, "depth" : 0.7 * mm});
        }
    });
